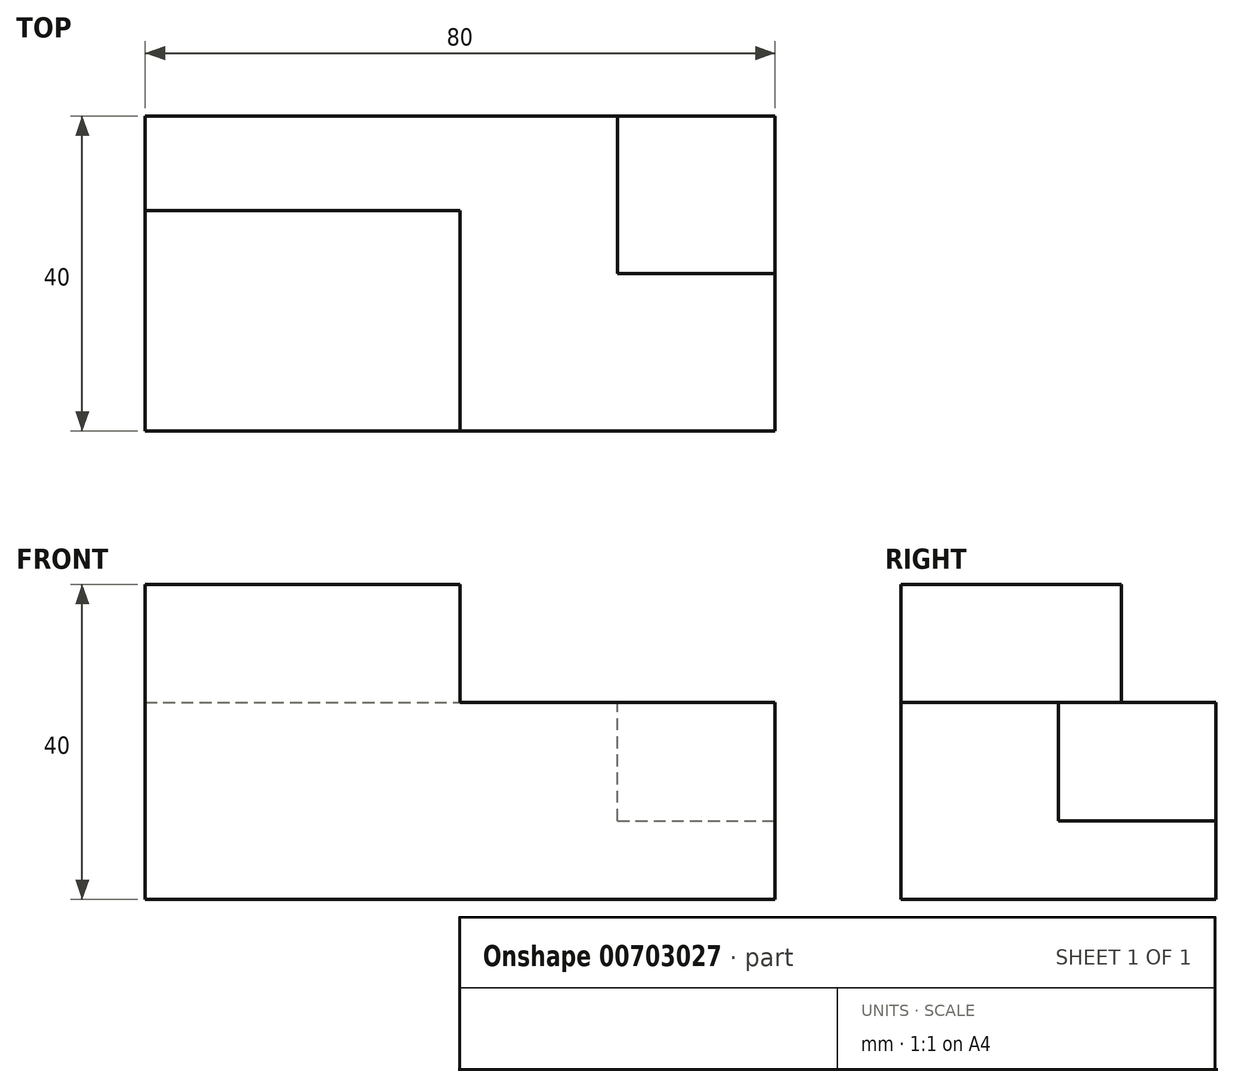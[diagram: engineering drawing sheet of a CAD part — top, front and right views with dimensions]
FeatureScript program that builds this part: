
annotation { "Feature Type Name" : "Feature", "Feature Type Description" : "" }
export const myFeature = defineFeature(function(context is Context, id is Id, definition is map)
    precondition{}
    {
        {
            var Q0;
            Q0=qCreatedBy(makeId("Front.planeOp"),FACE);
            var sketch = newSketch(context, id + "F0", { "sketchPlane" : qUnion([Q0])});
            skLineSegment(sketch, "E0.bottom", {"start": v(0, 0) * mm, "end": v(80, 0) * mm});
            skLineSegment(sketch, "E0.top", {"start": v(0, 25) * mm, "end": v(80, 25) * mm});
            skLineSegment(sketch, "E0.left", {"start": v(0, 0) * mm, "end": v(0, 25) * mm});
            skLineSegment(sketch, "E0.right", {"start": v(80, 0) * mm, "end": v(80, 25) * mm});
            skSolve(sketch);
        }
        {
            var Q0;
            Q0 = qSketchRegion(id + "F0", true);
            extrude(context, id + "F1", {"entities" : qUnion([Q0]), "depth" : 40 * mm, "offsetDistance" : 25.4 * mm});
        }
        {
            var Q0;
            Q0=makeQuery(id+"F1.opExtrude","SWEPT_FACE",FACE,{"disambiguationData":[OSD([sQuery(id+"F0.wireOp",EDGE,"E0.right")])]});
            var sketch = newSketch(context, id + "F2", { "sketchPlane" : qUnion([Q0])});
            skLineSegment(sketch, "E1.bottom", {"start": v(-20, 25) * mm, "end": v(0, 25) * mm});
            skLineSegment(sketch, "E1.top", {"start": v(-20, 10) * mm, "end": v(0, 10) * mm});
            skLineSegment(sketch, "E1.left", {"start": v(-20, 25) * mm, "end": v(-20, 10) * mm});
            skLineSegment(sketch, "E1.right", {"start": v(0, 25) * mm, "end": v(0, 10) * mm});
            skSolve(sketch);
        }
        {
            var Q0;
            Q0 = qSketchRegion(id + "F2", true);
            extrude(context, id + "F3", {"entities" : qUnion([Q0]), "operationType" : NewBodyOperationType.REMOVE, "oppositeDirection" : true, "depth" : 20 * mm, "offsetDistance" : 25.4 * mm});
        }
        {
            var Q0;
            Q0=makeQuery(id+"F1.opExtrude","SWEPT_FACE",FACE,{"disambiguationData":[OSD([sQuery(id+"F0.wireOp",EDGE,"E0.top")])]});
            var sketch = newSketch(context, id + "F4", { "sketchPlane" : qUnion([Q0])});
            skLineSegment(sketch, "E2.bottom", {"start": v(0, -40) * mm, "end": v(40, -40) * mm});
            skLineSegment(sketch, "E2.top", {"start": v(0, -12) * mm, "end": v(40, -12) * mm});
            skLineSegment(sketch, "E2.left", {"start": v(0, -40) * mm, "end": v(0, -12) * mm});
            skLineSegment(sketch, "E2.right", {"start": v(40, -40) * mm, "end": v(40, -12) * mm});
            skSolve(sketch);
        }
        {
            var Q0;
            Q0 = qSketchRegion(id + "F4", true);
            extrude(context, id + "F5", {"entities" : qUnion([Q0]), "operationType" : NewBodyOperationType.ADD, "depth" : 15 * mm, "offsetDistance" : 25.4 * mm});
        }
    });
